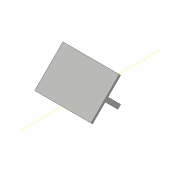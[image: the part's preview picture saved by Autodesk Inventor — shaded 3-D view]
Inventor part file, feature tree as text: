
AUTODESK INVENTOR PART (.ipt)
format: ipt  version: 2016 (Build 200138000, 138)  size: 326,656 bytes
history: native  units: mm
features: extrude x21, sketch x21, plane x5, projected_geometry x5, mirror x3, other x1
ambient origin geometry x8: Origin, YZ Plane, XZ Plane, XY Plane, X Axis, Y Axis, Z Axis, Center Point
bodies: 实体1 (feature_tree)
feature tree (56):
  extrude  "拉伸1"  Depth=200.0mm TaperAngle=0.0deg
  extrude  "拉伸3"  Depth=57.0mm TaperAngle=0.0deg
  extrude  "拉伸4"  Depth=10.0mm
  extrude  "拉伸5"  Depth=10.0mm
  extrude  "拉伸6"  Depth=200.0mm TaperAngle=0.0deg
  extrude  "拉伸7"  [1 undecoded]
  extrude  "拉伸8"  Depth=40.0mm
  plane  "工作平面4"
  extrude  "拉伸12"  Depth=20.0mm
  extrude  "拉伸17"  Depth=180.0mm TaperAngle=0.0deg
  extrude  "拉伸18"  Depth=42.0mm
  mirror  "镜像1"
  extrude  "拉伸19"  Depth=10.0mm TaperAngle=0.0deg
  plane  "工作平面6"
  mirror  "镜像2"
  plane  "工作平面7"
  mirror  "镜像3"
  extrude  "拉伸20"  Depth=40.0mm
  other  "工作轴1"
  extrude  "拉伸22"  Depth=18.0mm TaperAngle=0.0deg
  extrude  "拉伸23"  Depth=10.0mm TaperAngle=0.0deg
  extrude  "拉伸24"  Depth=15.0mm TaperAngle=0.0deg
  extrude  "拉伸25"  Depth=15.0mm TaperAngle=0.0deg
  extrude  "拉伸26"  Depth=10.0mm TaperAngle=0.0deg
  extrude  "拉伸27"  Depth=10.0mm TaperAngle=0.0deg
  extrude  "拉伸28"  [1 undecoded]
  extrude  "拉伸29"  [1 undecoded]
  extrude  "拉伸30"  [1 undecoded]
  sketch  "草图1"  dims[d1=10.0mm d2=200.0mm d3=0.0mm]
  sketch  "草图2"  dims[d4=57.0mm d7=57.0mm d8=0.0mm]
  sketch  "草图3"  dims[d9=200.0mm d10=0.0mm d11=10.0mm]
  sketch  "草图4"  dims[d12=200.0mm d13=0.0mm d14=10.0mm]
  sketch  "草图5"  dims[d15=200.0mm d16=0.0mm d17=200.0mm d18=0.0mm]
  sketch  "草图6"  dims[d19=200.0mm d20=0.0mm d30=-165.0mm]
  sketch  "草图7"  dims[d31=20.0mm d32=0.0mm d50=40.0mm]
  plane  "工作平面3"
  sketch  "草图11"  dims[d51=20.0mm d52=20.0mm]
  projected_geometry  "投影回路2"
  sketch  "草图17"  dims[d53=40.0mm d54=180.0mm d55=0.0mm]
  sketch  "草图18"  dims[d56=180.0mm d57=0.0mm d58=42.0mm]
  plane  "工作平面5"
  sketch  "草图19"  dims[d59=42.0mm d60=10.0mm d61=40.0mm d62=0.0mm d63=0.0mm]
  sketch  "草图20"  dims[d64=350.0mm d65=0.0mm d66=40.0mm]
  sketch  "草图21"  dims[d67=18.0mm d70=350.0mm d71=0.0mm]
  sketch  "草图22"  dims[d72=20.0mm d73=10.0mm d74=0.0mm]
  sketch  "草图23"  dims[d75=15.0mm d76=15.0mm d77=0.0mm]
  sketch  "草图24"  dims[d78=10.0mm d79=0.0mm d80=15.0mm d81=0.0mm]
  sketch  "草图25"  dims[d82=10.0mm d83=0.0mm d84=10.0mm d85=0.0mm]
  sketch  "草图26"  dims[d86=10.0mm d87=0.0mm d88=10.0mm d89=0.0mm]
  projected_geometry  "投影回路3"
  sketch  "草图27"
  projected_geometry  "投影回路4"
  sketch  "草图28"
  sketch  "草图29"
  projected_geometry  "投影回路5"
  projected_geometry  "投影回路6"
note: 4 required parameter values undecoded (feature->parameter linkage not recoverable at this tier; creation-order binding heuristic only, values carry confidence <= 0.55)
